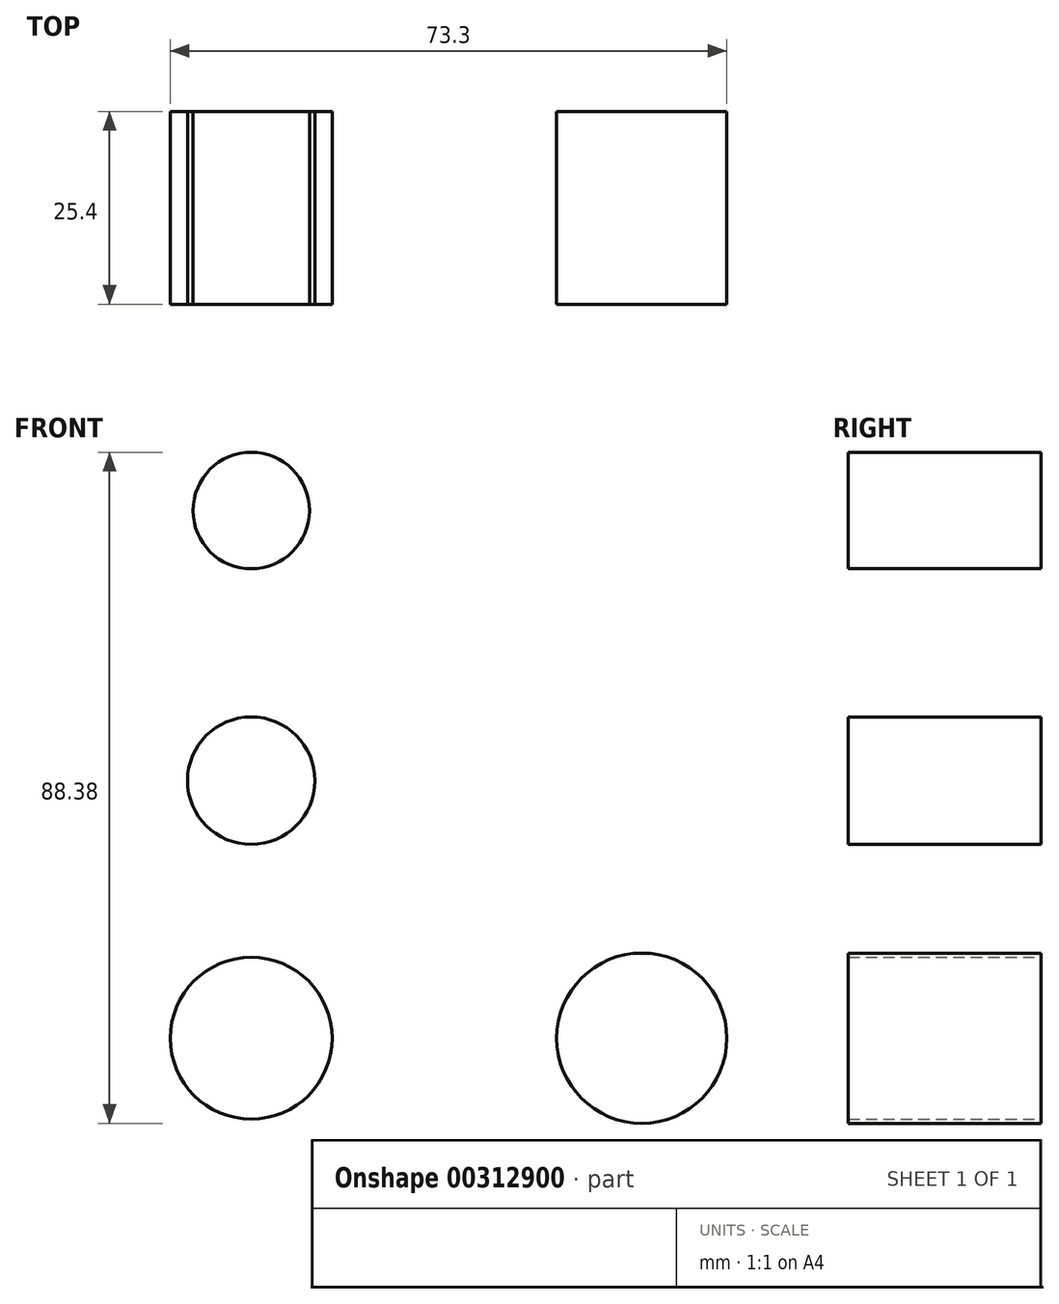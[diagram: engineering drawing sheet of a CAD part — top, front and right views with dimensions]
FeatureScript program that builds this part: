
annotation { "Feature Type Name" : "Feature", "Feature Type Description" : "" }
export const myFeature = defineFeature(function(context is Context, id is Id, definition is map)
    precondition{}
    {
        {
            var Q0;
            Q0=qCreatedBy(makeId("Front.planeOp"),FACE);
            var sketch = newSketch(context, id + "F0", { "sketchPlane" : qUnion([Q0])});
            skLineSegment(sketch, "E0", {"start": v(-51.44, 55.5) * mm, "end": v(-51.44, 19.91) * mm});
            skLineSegment(sketch, "E1", {"start": v(-51.44, 19.91) * mm, "end": v(-51.44, -14.01) * mm});
            skLineSegment(sketch, "E2", {"start": v(-51.44, -14.01) * mm, "end": v(0, -14.01) * mm});
            skCircle(sketch, "E3", {"center": v(-51.44, 55.5) * mm, "radius": 7.67 * mm});
            skCircle(sketch, "E4", {"center": v(-51.44, 19.91) * mm, "radius": 8.39 * mm});
            skCircle(sketch, "E5", {"center": v(-51.44, -14.01) * mm, "radius": 10.66 * mm});
            skCircle(sketch, "E6", {"center": v(0, -14.01) * mm, "radius": 11.2 * mm});
            skSolve(sketch);
        }
        {
            var Q0;
            Q0 = qSketchRegion(id + "F0", true);
            extrude(context, id + "F1", {"entities" : qUnion([Q0]), "depth" : 25.4 * mm});
        }
    });
